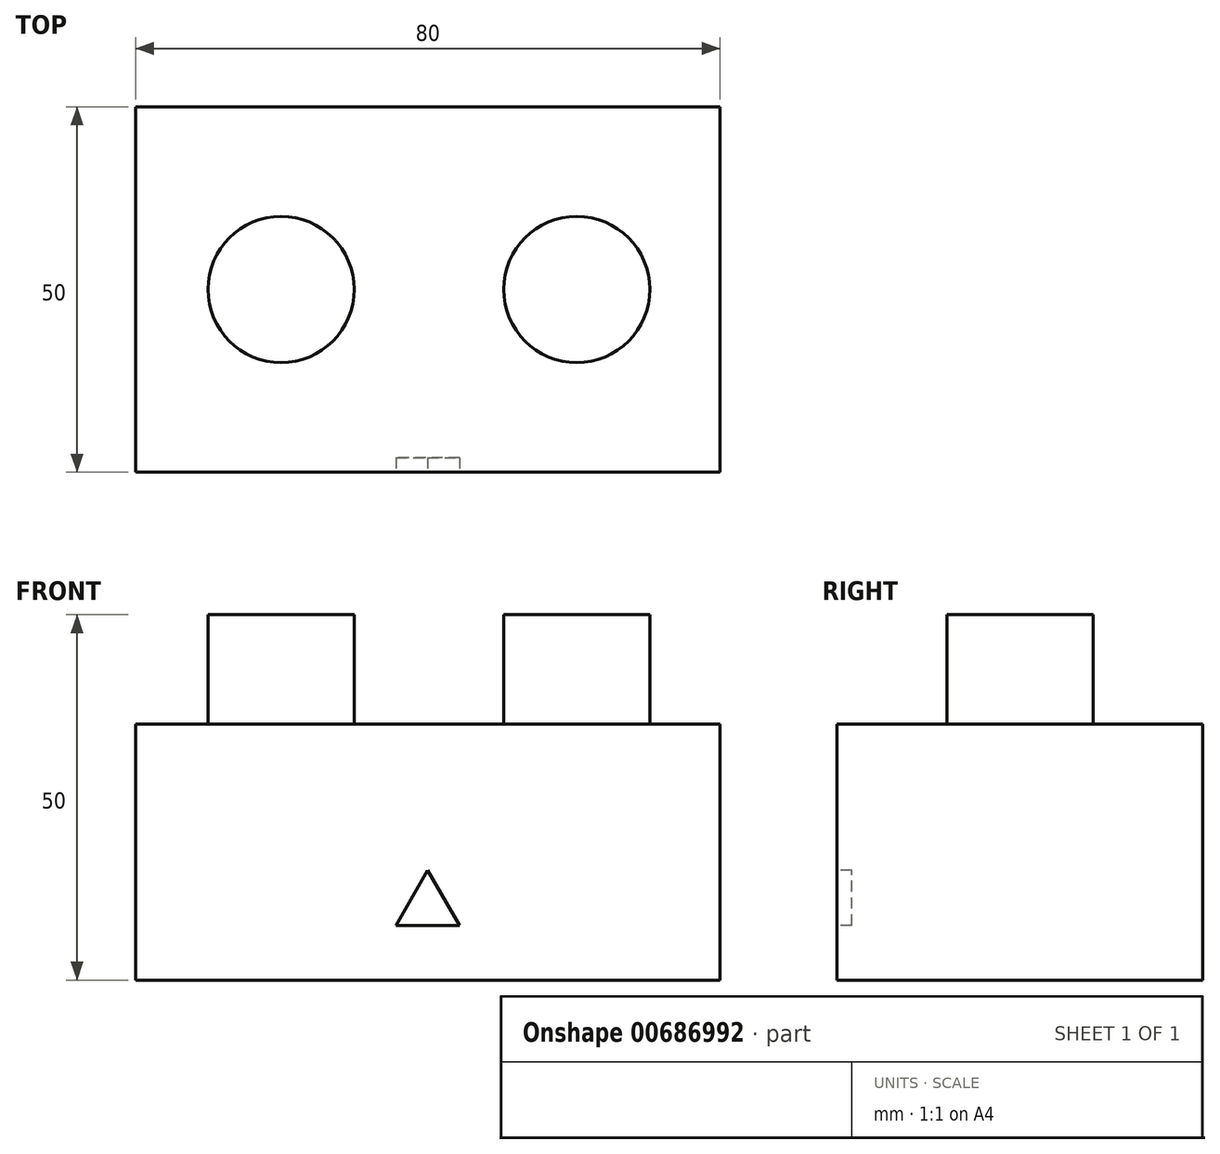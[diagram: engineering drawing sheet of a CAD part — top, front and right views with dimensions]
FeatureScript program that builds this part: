
annotation { "Feature Type Name" : "Feature", "Feature Type Description" : "" }
export const myFeature = defineFeature(function(context is Context, id is Id, definition is map)
    precondition{}
    {
        {
            var Q0;
            Q0=qCreatedBy(makeId("Top.planeOp"),FACE);
            var sketch = newSketch(context, id + "F0", { "sketchPlane" : qUnion([Q0])});
            skLineSegment(sketch, "E0.bottom", {"start": v(-40, 25) * mm, "end": v(40, 25) * mm});
            skLineSegment(sketch, "E0.top", {"start": v(-40, -25) * mm, "end": v(40, -25) * mm});
            skLineSegment(sketch, "E0.left", {"start": v(-40, 25) * mm, "end": v(-40, -25) * mm});
            skLineSegment(sketch, "E0.right", {"start": v(40, 25) * mm, "end": v(40, -25) * mm});
            skPoint(sketch, "E0.middle", {"position": v(0, 0) * mm});
            skSolve(sketch);
        }
        {
            var Q0;
            Q0=makeQuery(id+"F0.imprint","IMPRINT",FACE,{"disambiguationData":[TD([[makeQuery(id+"F0.imprint","IMPRINT",EDGE,{"derivedFrom":sQuery(id+"F0.wireOp",EDGE,"E0.bottom")}),-1.0]])]});
            extrude(context, id + "F1", {"entities" : qUnion([Q0]), "depth" : 35 * mm, "offsetDistance" : 25 * mm});
        }
        {
            var Q0;
            Q0=makeQuery(id+"F1.opExtrude","SWEPT_FACE",FACE,{"disambiguationData":[OSD([sQuery(id+"F0.wireOp",EDGE,"E0.top")])]});
            var sketch = newSketch(context, id + "F2", { "sketchPlane" : qUnion([Q0])});
            skCircle(sketch, "E1.cCircle", {"center": v(0, 10) * mm, "radius": 5 * mm, "construction": true});
            skLineSegment(sketch, "E1.0", {"start": v(-4.33, 7.5) * mm, "end": v(0, 15) * mm});
            skLineSegment(sketch, "E1.1", {"start": v(0, 15) * mm, "end": v(4.33, 7.5) * mm});
            skLineSegment(sketch, "E1.2", {"start": v(4.33, 7.5) * mm, "end": v(-4.33, 7.5) * mm});
            skSolve(sketch);
        }
        {
            var Q0;
            Q0 = qSketchRegion(id + "F2", true);
            extrude(context, id + "F3", {"entities" : qUnion([Q0]), "operationType" : NewBodyOperationType.REMOVE, "oppositeDirection" : true, "depth" : 2 * mm, "offsetDistance" : 25 * mm});
        }
        {
            var Q0;
            Q0=makeQuery(id+"F1.opExtrude","CAP_FACE",FACE,{"disambiguationData":[OSD([sQuery(id+"F0.wireOp",EDGE,"E0.bottom"),sQuery(id+"F0.wireOp",EDGE,"E0.top"),sQuery(id+"F0.wireOp",EDGE,"E0.left"),sQuery(id+"F0.wireOp",EDGE,"E0.right")])],"isStart":false});
            var sketch = newSketch(context, id + "F4", { "sketchPlane" : qUnion([Q0])});
            skCircle(sketch, "E2", {"center": v(-20.08, 0) * mm, "radius": 10 * mm});
            skCircle(sketch, "E3", {"center": v(20.37, 0) * mm, "radius": 10 * mm});
            skSolve(sketch);
        }
        {
            var Q0;
            Q0 = qSketchRegion(id + "F4", true);
            extrude(context, id + "F5", {"entities" : qUnion([Q0]), "operationType" : NewBodyOperationType.ADD, "depth" : 15 * mm, "offsetDistance" : 25 * mm});
        }
    });
